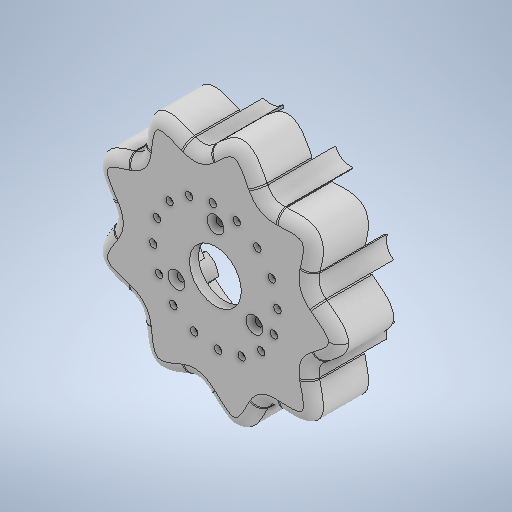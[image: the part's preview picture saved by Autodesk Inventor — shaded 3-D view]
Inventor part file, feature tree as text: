
AUTODESK INVENTOR PART (.ipt)
format: ipt  version: 2025 (Build 290162000, 162)  size: 1,257,472 bytes
history: native  units: mm
features: sketch x8, extrude x6, chamfer x1, fillet x1, other x1
ambient origin geometry x8: Origin, YZ Plane, XZ Plane, XY Plane, X Axis, Y Axis, Z Axis, Center Point
bodies: 实体1 (feature_tree)
feature tree (17):
  sketch  "草图1"  dims[d0=67.5mm d1=40.0mm]
  extrude  "拉伸1"  Depth=40.0mm
  extrude  "拉伸2"  Depth=30.0mm TaperAngle=360.0deg
  sketch  "草图2"  dims[d7=1.0mm d8=0.0mm d9=3600.0mm]
  extrude  "拉伸5"  Depth=3600.0mm TaperAngle=0.0deg
  extrude  "拉伸6"  Depth=4.0mm TaperAngle=0.0deg
  sketch  "草图4"  dims[d21=67.0mm]
  extrude  "拉伸7"  Depth=2.0mm TaperAngle=45.0deg
  chamfer  "倒角1"  Distance=96.0mm
  extrude  "拉伸8"  Depth=85.1mm
  fillet  "圆角2"  Radius=1.0mm
  sketch  "草图 - 环形阵列1"  dims[d2=3.4mm d3=30.0mm d5=360.0deg]
  other  "二维表达式曲线1"
  sketch  "草图 - 环形阵列2"  dims[d10=23.0mm d11=4.0mm d12=0.0mm]
  sketch  "草图3"  dims[d13=20.0mm d14=0.0mm d15=2.0mm d16=2.0mm d17=45.0deg]
  sketch  "草图 - 环形阵列3"  dims[d20=84.5mm]
  sketch  "草图 - 环形阵列5"  dims[d22=90.0mm d23=96.0mm d24=85.1mm d25=1.0mm d28=1.0mm d31=0.5mm d37=90.0mm d39=360.0deg d41=30.0mm d42=0.0mm d43=3.15mm d44=90.0mm d46=360.0deg d48=8.0mm d49=0.0mm d50=55.25mm d51=10.15mm d56=2.0mm d57=0.0mm d58=3.3mm d59=160.0mm d61=360.0deg d63=10.0mm d64=0.0mm d65=5.0mm]
